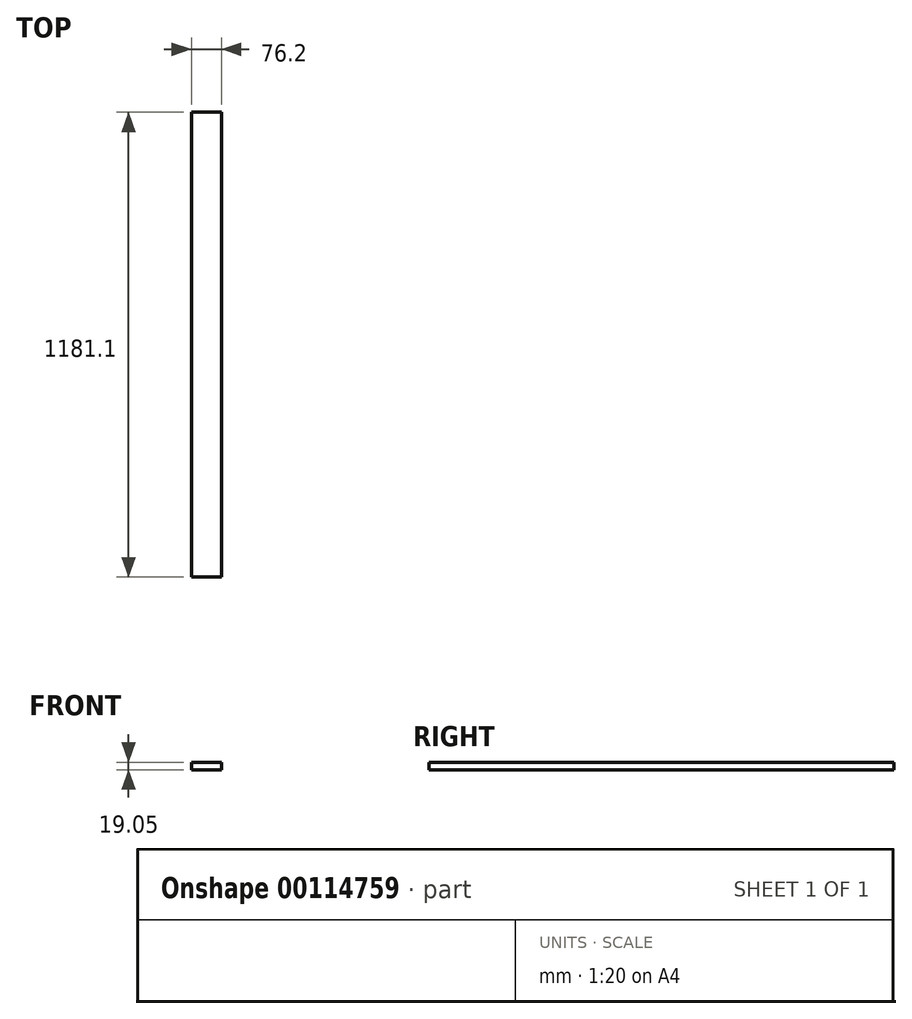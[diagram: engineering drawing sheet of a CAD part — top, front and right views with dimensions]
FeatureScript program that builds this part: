
annotation { "Feature Type Name" : "Feature", "Feature Type Description" : "" }
export const myFeature = defineFeature(function(context is Context, id is Id, definition is map)
    precondition{}
    {
        {
            var Q0;
            Q0=qCreatedBy(makeId("Top.planeOp"),FACE);
            var sketch = newSketch(context, id + "F0", { "sketchPlane" : qUnion([Q0])});
            skLineSegment(sketch, "E0.bottom", {"start": v(0, 0) * mm, "end": v(76.2, 0) * mm});
            skLineSegment(sketch, "E0.top", {"start": v(0, 1181.1) * mm, "end": v(76.2, 1181.1) * mm});
            skLineSegment(sketch, "E0.left", {"start": v(0, 0) * mm, "end": v(0, 1181.1) * mm});
            skLineSegment(sketch, "E0.right", {"start": v(76.2, 0) * mm, "end": v(76.2, 1181.1) * mm});
            skSolve(sketch);
        }
        {
            var Q0;
            Q0=qSketchRegion(id+"F0",true);
            extrude(context, id + "F1", {"entities" : qUnion([Q0]), "depth" : 19.05 * mm});
        }
    });
